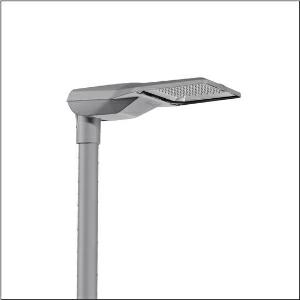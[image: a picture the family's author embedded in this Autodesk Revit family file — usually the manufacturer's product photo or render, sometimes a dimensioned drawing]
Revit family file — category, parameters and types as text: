
# Revit family: streetlight_sl_21_iq_midi___st1_5a_5xe3p41d08mb_62ad
name_source: partatom
category: Lighting Fixtures
units: mm (PartAtom-declared; Revit-internal decimal feet)

## family parameters
Cut with Voids When Loaded = No
Host = Face
Light Source = No
Part Type = Normal
Room Calculation Point = No
Round Connector Dimension = Use Diameter
Shared = No

## types (1)
- --- (1 x LED, 20000 lm, 146.7 W, 4000K)
    Apparent Load = 147 VA
    CIE Flux Codes = 22 53 95 100 100
    Color Rendering = 70
    Color Temperature = 4000K
    Default Elevation = 1800 mm
    Description = Streetlight SL 21 iQ midi, mast luminaire, primary light control with lens, of PMMA, primary optical cover: cover, of toughened safety glass, transparent, light distribution: ST1.5a, light emission: direct distribution, primary light characteristic: asymmetric, installation type: post-top, side-entry, LED, High Power LED, rated luminous flux: 20.000lm, luminous efficacy: 136lm/W, light colour: 740, colour temperature: 4000K, control: Auto-Match, Temp-Guard, Lumen-Switch, Night-Set, Smart-Wire, Light-Fading, Desk-Remote (wireless, voltage-free reading and setting of iQ features in the workshop via application-optimized NFC function/RFID function), optimised constant luminous flux control (CLO 2.0), presetting dimming linear, mains connection: 230..240V, AC, 50/60Hz, start of lifetime: 147W, end of service life: 161W, reduction: 62W, luminaire housing, of diecast aluminium, powder-coated, Siteco® metallic grey (DB 702S), corrosivity category C5 mid according to DIN EN ISO 12944, please order mast flange separately, inclination adjustable: 0°, 5°, 10°, 15°, sealing non-destructively replaceable, multi-level sealing system, length: 644mm, width: 335mm, height: 110mm, mast flange for spigot size: 42mm (side-entry): 5XC10008XM4, 60/48mm (side-entry/post-top): 5XC10108XM2, 76/60mm (side-entry/post-top): 5XC10108XM1, protection rating (complete): IP66, insulation class (complete): insulation class II (safety insulation), certification: CE, ENEC, ENEC+, VDE, impact resistance: IK09, permissible operating ambient temperature for outdoor applications: -40..+50°C, standard-compliant lighting for roads and squares, packaging unit: 1 piece

Light Distribution: ST1.5a
    Height = 111 mm
    Lamp = 1 x LED
    Lamp Light Flux = 20000 lm
    Lamp Power = 146.7 W
    Lamp count = 1
    Length = 644 mm
    Luminous efficacy = 136 lm/W
    Manufacturer = Siteco
    ModVariant = No
    Model = 5XE3P41D08MB
    Number of Poles = 1
    OnlyDefault = Yes
    Power Factor = 1
    Product Name = Streetlight SL 21 iQ midi | ST1.5a
    Product group = mast luminaire | pylon top
    ProductGroupID = 6100
    Protection Class = Protection class II
    Protection Degree = IP 66
    RLX_Detail_Level = 1
    RLX_Emergency_Light_Flux = 0 lm
    RLX_Emergency_Type = 0
    RLX_Emergency_Type_DB = No
    RlxData = <blob elided: 94117 chars, md5=d9970efd>
    Socket = socket
    Standby Power = 0 W
    System Light Flux = 20000 lm
    System Power = 147 W
    Type Comments = factory setting: luminous flux: 100 % | dim-lin: 254 | 753 mA
    Type Image = l_1004298.jpg
    URL = http://relux.com
    VarID = @adj_127413
    Voltage = 0 V
    Weight = 0.00 kg
    Width = 336 mm

## geometry (parser evidence)
native form markers: Blend x4, Sweep x10
no freeform markers — native parametric forms only
